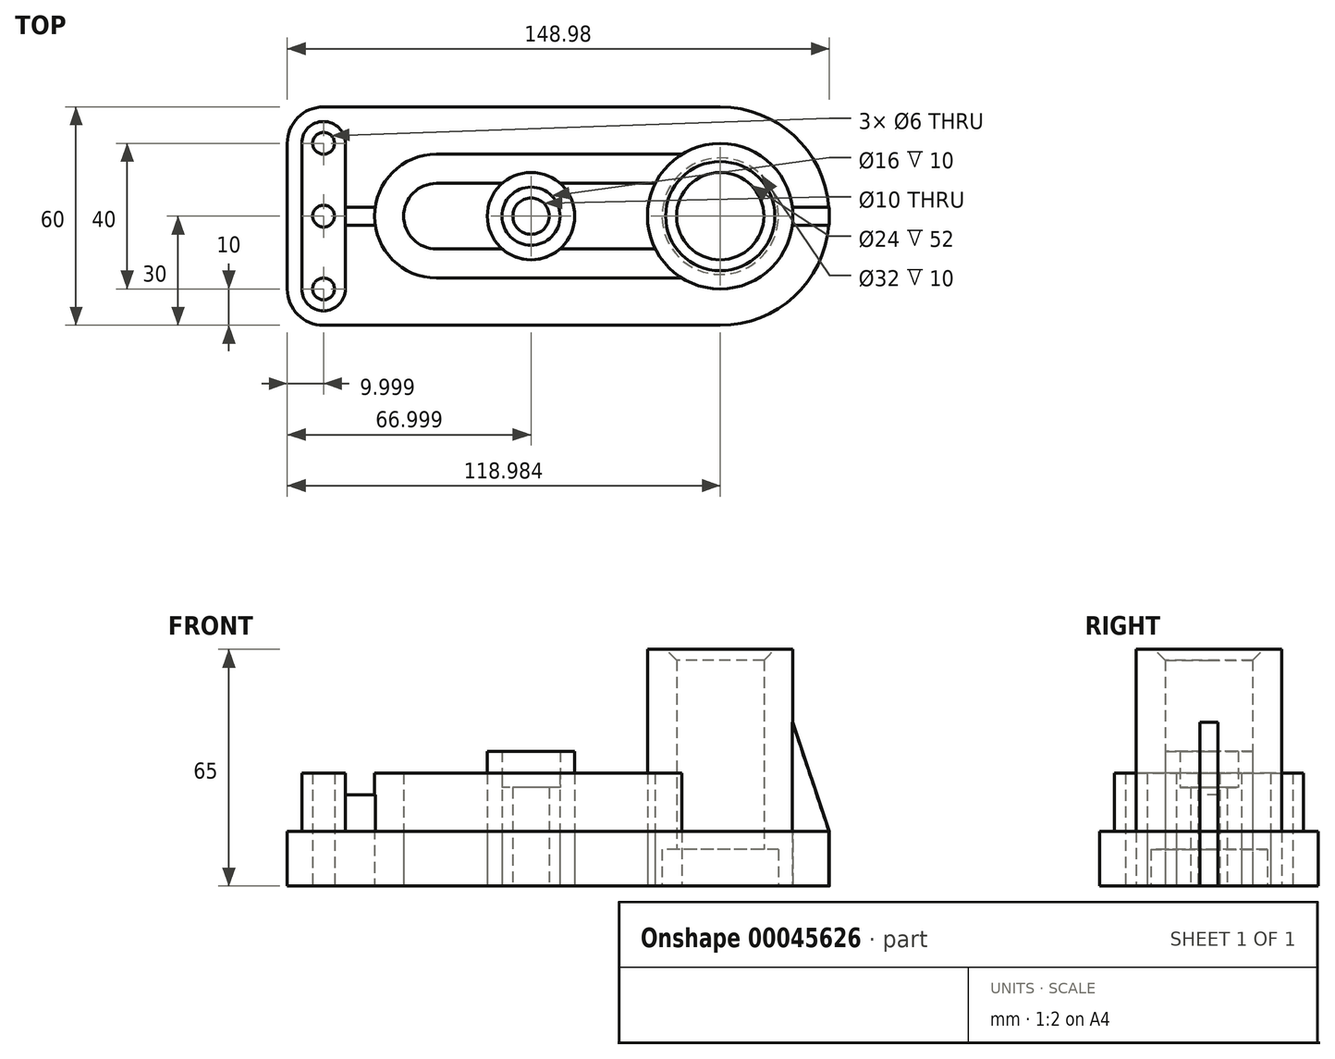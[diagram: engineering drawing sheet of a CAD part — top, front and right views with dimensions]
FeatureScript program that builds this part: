
annotation { "Feature Type Name" : "Feature", "Feature Type Description" : "" }
export const myFeature = defineFeature(function(context is Context, id is Id, definition is map)
    precondition{}
    {
        {
            var Q0;
            Q0=qCreatedBy(makeId("Top.planeOp"),FACE);
            var sketch = newSketch(context, id + "F0", { "sketchPlane" : qUnion([Q0])});
            skLineSegment(sketch, "E0", {"start": v(-87.4, 0) * mm, "end": v(91.32, 0) * mm, "construction": true});
            skLineSegment(sketch, "E1", {"start": v(-85.9, 0) * mm, "end": v(-85.9, -20) * mm});
            skArc(sketch, "E2", {"start": v(-85.9, -20) * mm, "mid": v(-82.97, -27.07) * mm, "end": v(-75.9, -30) * mm});
            skCircle(sketch, "E3", {"center": v(-75.9, -20) * mm, "radius": 3 * mm});
            skArc(sketch, "E4", {"start": v(-81.9, -20) * mm, "mid": v(-75.9, -26) * mm, "end": v(-69.9, -20) * mm});
            skLineSegment(sketch, "E5", {"start": v(-81.9, -20) * mm, "end": v(-81.9, 0) * mm});
            skLineSegment(sketch, "E6", {"start": v(-69.9, -20) * mm, "end": v(-69.9, 0) * mm});
            skArc(sketch, "E7", {"start": v(-78.9, 0) * mm, "mid": v(-75.9, -3) * mm, "end": v(-72.9, 0) * mm});
            skLineSegment(sketch, "E8", {"start": v(-75.9, -30) * mm, "end": v(33.1, -30) * mm});
            skArc(sketch, "E9", {"start": v(-61.9, 0) * mm, "mid": v(-56.92, -12.02) * mm, "end": v(-44.9, -17) * mm});
            skArc(sketch, "E10", {"start": v(-53.9, 0) * mm, "mid": v(-51.27, -6.36) * mm, "end": v(-44.9, -9) * mm});
            skArc(sketch, "E11", {"start": v(-23.9, 0) * mm, "mid": v(-18.9, -5) * mm, "end": v(-13.9, 0) * mm});
            skArc(sketch, "E12", {"start": v(-26.9, 0) * mm, "mid": v(-18.9, -8) * mm, "end": v(-10.9, 0) * mm});
            skArc(sketch, "E13", {"start": v(-30.9, 0) * mm, "mid": v(-18.9, -12) * mm, "end": v(-6.9, 0) * mm});
            skPoint(sketch, "E14", {"position": v(-30.9, 0) * mm});
            skPoint(sketch, "E15", {"position": v(-6.9, 0) * mm});
            skLineSegment(sketch, "E16", {"start": v(-44.9, -9) * mm, "end": v(-26.84, -9) * mm});
            skArc(sketch, "E17", {"start": v(21.08, 0) * mm, "mid": v(33.08, -12) * mm, "end": v(45.08, 0) * mm});
            skArc(sketch, "E18", {"start": v(17.08, 0) * mm, "mid": v(33.08, -16) * mm, "end": v(49.08, 0) * mm});
            skArc(sketch, "E19", {"start": v(13.08, 0) * mm, "mid": v(33.08, -20) * mm, "end": v(53.08, 0) * mm});
            skLineSegment(sketch, "E20", {"start": v(-10.96, -9) * mm, "end": v(15.22, -9) * mm});
            skLineSegment(sketch, "E21", {"start": v(-44.9, -17) * mm, "end": v(22.55, -17) * mm});
            skArc(sketch, "E22", {"start": v(33.1, -30) * mm, "mid": v(54.3, -21.2) * mm, "end": v(63.08, 0) * mm});
            skLineSegment(sketch, "E23.MirrorCS", {"start": v(-85.9, 0) * mm, "end": v(-85.9, 20) * mm});
            skLineSegment(sketch, "E24.MirrorCS", {"start": v(-81.9, 20) * mm, "end": v(-81.9, 0) * mm});
            skArc(sketch, "E25.MirrorCS", {"start": v(-85.9, 20) * mm, "mid": v(-82.97, 27.07) * mm, "end": v(-75.9, 30) * mm});
            skArc(sketch, "E26.MirrorCS", {"start": v(-81.9, 20) * mm, "mid": v(-75.9, 26) * mm, "end": v(-69.9, 20) * mm});
            skCircle(sketch, "E27.MirrorC", {"center": v(-75.9, 20) * mm, "radius": 3 * mm});
            skLineSegment(sketch, "E28.MirrorCS", {"start": v(-69.9, 20) * mm, "end": v(-69.9, 0) * mm});
            skArc(sketch, "E29.MirrorCS", {"start": v(-78.9, 0) * mm, "mid": v(-75.9, 3) * mm, "end": v(-72.9, 0) * mm});
            skLineSegment(sketch, "E30.MirrorCS", {"start": v(-75.9, 30) * mm, "end": v(33.1, 30) * mm});
            skArc(sketch, "E31.MirrorCS", {"start": v(-61.9, 0) * mm, "mid": v(-56.92, 12.02) * mm, "end": v(-44.9, 17) * mm});
            skArc(sketch, "E32.MirrorCS", {"start": v(-53.9, 0) * mm, "mid": v(-51.27, 6.36) * mm, "end": v(-44.9, 9) * mm});
            skLineSegment(sketch, "E33.MirrorCS", {"start": v(-44.9, 9) * mm, "end": v(-26.84, 9) * mm});
            skLineSegment(sketch, "E34.MirrorCS", {"start": v(-44.9, 17) * mm, "end": v(22.55, 17) * mm});
            skArc(sketch, "E35.MirrorCS", {"start": v(-30.9, 0) * mm, "mid": v(-18.9, 12) * mm, "end": v(-6.9, 0) * mm});
            skArc(sketch, "E36.MirrorCS", {"start": v(-26.9, 0) * mm, "mid": v(-18.9, 8) * mm, "end": v(-10.9, 0) * mm});
            skArc(sketch, "E37.MirrorCS", {"start": v(-23.9, 0) * mm, "mid": v(-18.9, 5) * mm, "end": v(-13.9, 0) * mm});
            skLineSegment(sketch, "E38.MirrorCS", {"start": v(-10.96, 9) * mm, "end": v(15.22, 9) * mm});
            skArc(sketch, "E39.MirrorCS", {"start": v(13.08, 0) * mm, "mid": v(33.08, 20) * mm, "end": v(53.08, 0) * mm});
            skArc(sketch, "E40.MirrorCS", {"start": v(17.08, 0) * mm, "mid": v(33.08, 16) * mm, "end": v(49.08, 0) * mm});
            skArc(sketch, "E41.MirrorCS", {"start": v(21.08, 0) * mm, "mid": v(33.08, 12) * mm, "end": v(45.08, 0) * mm});
            skArc(sketch, "E42.MirrorCS", {"start": v(33.1, 30) * mm, "mid": v(54.3, 21.2) * mm, "end": v(63.08, 0) * mm});
            skLineSegment(sketch, "E43", {"start": v(-69.9, -2.5) * mm, "end": v(-61.72, -2.5) * mm});
            skLineSegment(sketch, "E44.MirrorCS", {"start": v(-69.9, 2.5) * mm, "end": v(-61.72, 2.5) * mm});
            skLineSegment(sketch, "E45", {"start": v(52.93, -2.5) * mm, "end": v(62.98, -2.5) * mm});
            skLineSegment(sketch, "E46", {"start": v(52.93, 2.5) * mm, "end": v(62.98, 2.5) * mm});
            skSolve(sketch);
        }
        {
            var Q0;
            Q0=makeQuery(id+"F0.imprint","IMPRINT",FACE,{"disambiguationData":[TD([[makeQuery(id+"F0.imprint","IMPRINT",EDGE,{"derivedFrom":sQuery(id+"F0.wireOp",EDGE,"E1")}),1.0]])]});
            var Q1;
            Q1=makeQuery(id+"F0.imprint","IMPRINT",FACE,{"disambiguationData":[TD([[makeQuery(id+"F0.imprint","IMPRINT",EDGE,{"derivedFrom":sQuery(id+"F0.wireOp",EDGE,"E10")}),1.0]])]});
            var Q2;
            {var subQ5=sQuery(id+"F0.wireOp",EDGE,"E20");Q2=makeQuery(id+"F0.imprint","IMPRINT",FACE,{"disambiguationData":[TD([[makeQuery(id+"F0.imprint","IMPRINT",EDGE,{"derivedFrom":subQ5}),1.0]])]});}
            extrude(context, id + "F1", {"entities" : qUnion([Q0, Q1, Q2]), "depth" : 15 * mm});
        }
        {
            var Q0;
            Q0=makeQuery(id+"F0.imprint","IMPRINT",FACE,{"disambiguationData":[TD([[makeQuery(id+"F0.imprint","IMPRINT",EDGE,{"derivedFrom":sQuery(id+"F0.wireOp",EDGE,"E3")}),-1.0]])]});
            extrude(context, id + "F2", {"entities" : qUnion([Q0]), "operationType" : NewBodyOperationType.ADD, "depth" : 31 * mm});
        }
        {
            var Q0;
            {var subQ2=sQuery(id+"F0.wireOp",EDGE,"E43");Q0=makeQuery(id+"F0.imprint","IMPRINT",FACE,{"disambiguationData":[TD([[makeQuery(id+"F0.imprint","IMPRINT",EDGE,{"derivedFrom":subQ2}),1.0]])]});}
            extrude(context, id + "F3", {"entities" : qUnion([Q0]), "operationType" : NewBodyOperationType.ADD, "depth" : 25 * mm});
        }
        {
            var Q0;
            Q0=makeQuery(id+"F0.imprint","IMPRINT",FACE,{"disambiguationData":[TD([[makeQuery(id+"F0.imprint","IMPRINT",EDGE,{"derivedFrom":sQuery(id+"F0.wireOp",EDGE,"E10")}),-1.0]])]});
            extrude(context, id + "F4", {"entities" : qUnion([Q0]), "depth" : 31 * mm});
        }
        {
            var Q0;
            Q0=makeQuery(id+"F0.imprint","IMPRINT",FACE,{"disambiguationData":[TD([[makeQuery(id+"F0.imprint","IMPRINT",EDGE,{"derivedFrom":sQuery(id+"F0.wireOp",EDGE,"E12")}),-1.0]])]});
            extrude(context, id + "F5", {"entities" : qUnion([Q0]), "depth" : 37 * mm});
        }
        {
            var Q0;
            Q0=makeQuery(id+"F0.imprint","IMPRINT",FACE,{"disambiguationData":[TD([[makeQuery(id+"F0.imprint","IMPRINT",EDGE,{"derivedFrom":sQuery(id+"F0.wireOp",EDGE,"E11")}),-1.0]])]});
            extrude(context, id + "F6", {"entities" : qUnion([Q0]), "operationType" : NewBodyOperationType.ADD, "depth" : 27 * mm});
        }
        {
            var Q0;
            Q0=makeQuery(id+"F0.imprint","IMPRINT",FACE,{"disambiguationData":[TD([[makeQuery(id+"F0.imprint","IMPRINT",EDGE,{"derivedFrom":sQuery(id+"F0.wireOp",EDGE,"E18")}),-1.0]])]});
            var Q1;
            Q1=makeQuery(id+"F0.imprint","IMPRINT",FACE,{"disambiguationData":[TD([[makeQuery(id+"F0.imprint","IMPRINT",EDGE,{"derivedFrom":sQuery(id+"F0.wireOp",EDGE,"E17")}),-1.0]])]});
            extrude(context, id + "F7", {"entities" : qUnion([Q0, Q1]), "depth" : 65 * mm});
        }
        {
            var Q0;
            Q0=makeQuery(id+"F0.imprint","IMPRINT",FACE,{"disambiguationData":[TD([[makeQuery(id+"F0.imprint","IMPRINT",EDGE,{"derivedFrom":sQuery(id+"F0.wireOp",EDGE,"E17")}),-1.0]])]});
            extrude(context, id + "F8", {"entities" : qUnion([Q0]), "operationType" : NewBodyOperationType.REMOVE, "depth" : 10 * mm});
        }
        {
            var Q0;
            Q0=makeQuery(id+"F7.opExtrude","CAP_EDGE",EDGE,{"disambiguationData":[OSD([sQuery(id+"F0.wireOp",EDGE,"E17"),sQuery(id+"F0.wireOp",EDGE,"E41.MirrorCS")])],"isStart":false});
            chamfer(context, id + "F9", {"entities" : qUnion([Q0]), "chamferType" : ChamferType.OFFSET_ANGLE, "width" : 3 * mm, "oppositeDirection" : false, "angle" : 45 * degree, "tangentPropagation" : true});
        }
        {
            var Q0;
            {var subQ2=sQuery(id+"F0.wireOp",EDGE,"E45");Q0=makeQuery(id+"F0.imprint","IMPRINT",FACE,{"disambiguationData":[TD([[makeQuery(id+"F0.imprint","IMPRINT",EDGE,{"derivedFrom":subQ2}),1.0]])]});}
            extrude(context, id + "F10", {"entities" : qUnion([Q0]), "depth" : 45 * mm});
        }
        {
            var Q0;
            Q0=makeQuery(id+"F10.opExtrude","CAP_EDGE",EDGE,{"disambiguationData":[OSD([sQuery(id+"F0.wireOp",EDGE,"E22"),sQuery(id+"F0.wireOp",EDGE,"E42.MirrorCS")])],"isStart":false});
            chamfer(context, id + "F11", {"entities" : qUnion([Q0]), "chamferType" : ChamferType.TWO_OFFSETS, "width1" : 10 * mm, "oppositeDirection" : false, "width2" : 30 * mm, "tangentPropagation" : true});
        }
    });
